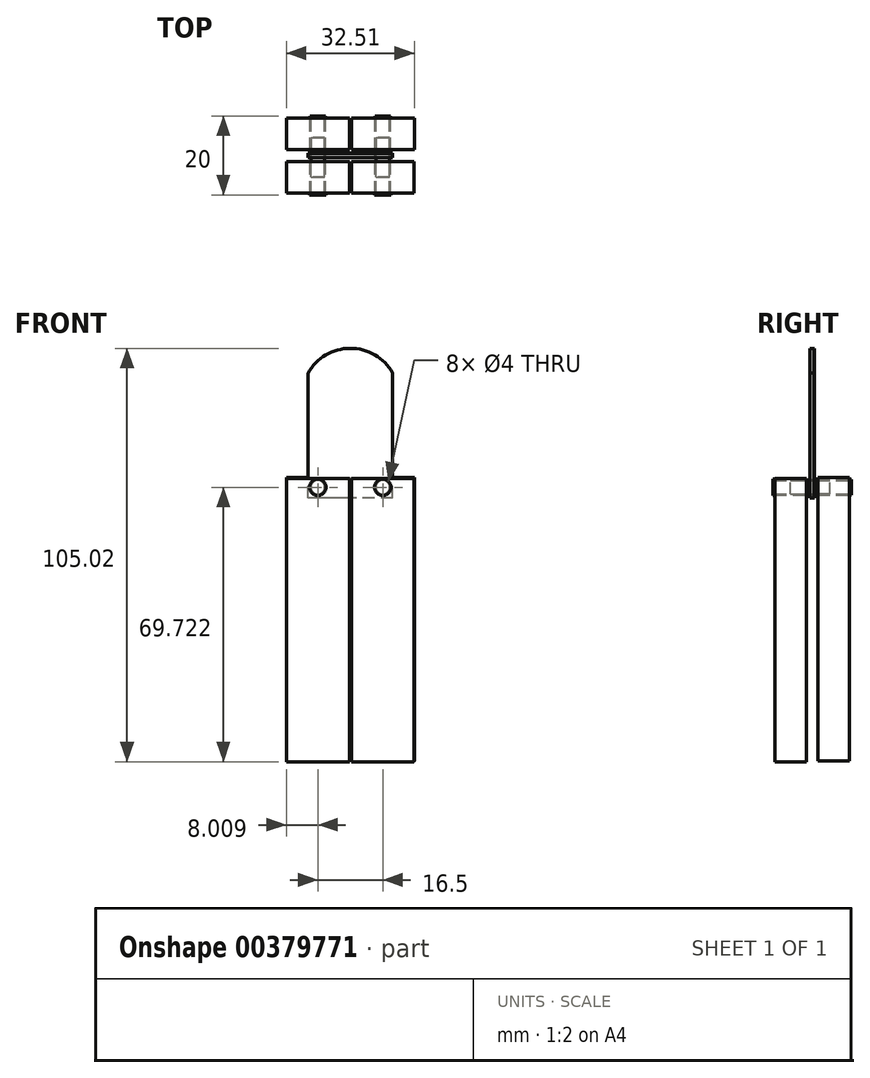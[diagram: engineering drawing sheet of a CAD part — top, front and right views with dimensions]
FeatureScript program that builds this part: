
annotation { "Feature Type Name" : "Feature", "Feature Type Description" : "" }
export const myFeature = defineFeature(function(context is Context, id is Id, definition is map)
    precondition{}
    {
        {
            var Q0;
            Q0=qCreatedBy(makeId("Front.planeOp"),FACE);
            var sketch = newSketch(context, id + "F0", { "sketchPlane" : qUnion([Q0])});
            skLineSegment(sketch, "E0.bottom", {"start": v(-36.14, 39.08) * mm, "end": v(-20.14, 39.08) * mm});
            skLineSegment(sketch, "E0.top", {"start": v(-36.14, -32.92) * mm, "end": v(-20.14, -32.92) * mm});
            skLineSegment(sketch, "E0.left", {"start": v(-36.14, 39.08) * mm, "end": v(-36.14, -32.92) * mm});
            skLineSegment(sketch, "E0.right", {"start": v(-20.14, 39.08) * mm, "end": v(-20.14, -32.92) * mm});
            skLineSegment(sketch, "E1.bottom", {"start": v(-19.64, 39.08) * mm, "end": v(-3.64, 39.08) * mm});
            skLineSegment(sketch, "E1.top", {"start": v(-19.64, -32.92) * mm, "end": v(-3.64, -32.92) * mm});
            skLineSegment(sketch, "E1.left", {"start": v(-19.64, 39.08) * mm, "end": v(-19.64, -32.92) * mm});
            skLineSegment(sketch, "E1.right", {"start": v(-3.64, 39.08) * mm, "end": v(-3.64, -32.92) * mm});
            skSolve(sketch);
        }
        {
            var Q0;
            Q0=makeQuery(id+"F0.imprint","IMPRINT",FACE,{"disambiguationData":[TD([[makeQuery(id+"F0.imprint","IMPRINT",EDGE,{"derivedFrom":sQuery(id+"F0.wireOp",EDGE,"E0.bottom")}),-1.0]])]});
            var Q1;
            Q1=makeQuery(id+"F0.imprint","IMPRINT",FACE,{"disambiguationData":[TD([[makeQuery(id+"F0.imprint","IMPRINT",EDGE,{"derivedFrom":sQuery(id+"F0.wireOp",EDGE,"E1.bottom")}),-1.0]])]});
            extrude(context, id + "F1", {"entities" : qUnion([Q0, Q1]), "depth" : 8 * mm});
        }
        {
            var Q0;
            Q0=makeQuery(id+"F1.opExtrude","CAP_FACE",FACE,{"disambiguationData":[OSD([sQuery(id+"F0.wireOp",EDGE,"E1.bottom"),sQuery(id+"F0.wireOp",EDGE,"E1.top"),sQuery(id+"F0.wireOp",EDGE,"E1.left"),sQuery(id+"F0.wireOp",EDGE,"E1.right")])],"isStart":true});
            var sketch = newSketch(context, id + "F2", { "sketchPlane" : qUnion([Q0])});
            skCircle(sketch, "E2", {"center": v(11.64, 36.58) * mm, "radius": 1.5 * mm});
            skCircle(sketch, "E3", {"center": v(28.14, 36.58) * mm, "radius": 1.5 * mm});
            skCircle(sketch, "E4", {"center": v(28.14, 36.58) * mm, "radius": 1.75 * mm});
            skCircle(sketch, "E5", {"center": v(11.64, 36.58) * mm, "radius": 1.75 * mm});
            skCircle(sketch, "E6", {"center": v(11.64, 36.58) * mm, "radius": 2 * mm});
            skCircle(sketch, "E7", {"center": v(28.14, 36.58) * mm, "radius": 2 * mm});
            skSolve(sketch);
        }
        {
            var Q0;
            Q0 = qSketchRegion(id + "F2", true);
            extrude(context, id + "F3", {"entities" : qUnion([Q0]), "oppositeDirection" : true, "depth" : 11 * mm});
        }
        {
            var Q0;
            Q0=qCreatedBy(makeId("Front.planeOp"),FACE);
            cPlane(context, id + "F4", {"entities" : qUnion([Q0]), "cplaneType" : CPlaneType.OFFSET, "offset" : 9 * mm, "width" : 150 * mm, "height" : 150 * mm});
        }
        {
            var Q0;
            Q0=qCreatedBy(id+"F4.planeOp",FACE);
            var sketch = newSketch(context, id + "F5", { "sketchPlane" : qUnion([Q0])});
            skLineSegment(sketch, "E8", {"start": v(-30.64, 33.85) * mm, "end": v(-30.64, 65.54) * mm});
            skLineSegment(sketch, "E9", {"start": v(-9.14, 33.88) * mm, "end": v(-9.14, 65.6) * mm});
            skArc(sketch, "E10", {"start": v(-9.14, 65.6) * mm, "mid": v(-19.9, 71.88) * mm, "end": v(-30.64, 65.54) * mm});
            skLineSegment(sketch, "E11", {"start": v(-9.14, 33.88) * mm, "end": v(-30.64, 33.88) * mm});
            skLineSegment(sketch, "E12", {"start": v(-30.64, 33.85) * mm, "end": v(-30.64, 33.88) * mm});
            skSolve(sketch);
        }
        {
            var Q0;
            Q0=makeQuery(id+"F5.imprint","IMPRINT",FACE,{"disambiguationData":[TD([[makeQuery(id+"F5.imprint","IMPRINT",EDGE,{"derivedFrom":sQuery(id+"F5.wireOp",EDGE,"E8")}),-1.0]])]});
            extrude(context, id + "F6", {"entities" : qUnion([Q0]), "operationType" : NewBodyOperationType.ADD, "depth" : 1 * mm});
        }
        {
            var Q0;
            Q0=qCreatedBy(id+"F4.planeOp",FACE);
            cPlane(context, id + "F7", {"entities" : qUnion([Q0]), "cplaneType" : CPlaneType.OFFSET, "offset" : 2 * mm, "width" : 150 * mm, "height" : 150 * mm});
        }
        {
            var Q0;
            Q0=qCreatedBy(id+"F7.planeOp",FACE);
            cPlane(context, id + "F8", {"entities" : qUnion([Q0]), "cplaneType" : CPlaneType.OFFSET, "offset" : 10 * mm, "width" : 150 * mm, "height" : 150 * mm});
        }
        {
            var Q0;
            Q0=qCreatedBy(id+"F8.planeOp",FACE);
            var sketch = newSketch(context, id + "F9", { "sketchPlane" : qUnion([Q0])});
            skLineSegment(sketch, "E13.bottom", {"start": v(-36.15, 38.86) * mm, "end": v(-20.15, 38.86) * mm});
            skLineSegment(sketch, "E13.top", {"start": v(-36.15, -33.14) * mm, "end": v(-20.15, -33.14) * mm});
            skLineSegment(sketch, "E13.left", {"start": v(-36.15, 38.86) * mm, "end": v(-36.15, -33.14) * mm});
            skLineSegment(sketch, "E13.right", {"start": v(-20.15, 38.86) * mm, "end": v(-20.15, -33.14) * mm});
            skLineSegment(sketch, "E14.bottom", {"start": v(-3.65, 38.86) * mm, "end": v(-19.65, 38.86) * mm});
            skLineSegment(sketch, "E14.top", {"start": v(-3.65, -33.14) * mm, "end": v(-19.65, -33.14) * mm});
            skLineSegment(sketch, "E14.left", {"start": v(-3.65, 38.86) * mm, "end": v(-3.65, -33.14) * mm});
            skLineSegment(sketch, "E14.right", {"start": v(-19.65, 38.86) * mm, "end": v(-19.65, -33.14) * mm});
            skSolve(sketch);
        }
        {
            var Q0;
            Q0=makeQuery(id+"F9.imprint","IMPRINT",FACE,{"disambiguationData":[TD([[makeQuery(id+"F9.imprint","IMPRINT",EDGE,{"derivedFrom":sQuery(id+"F9.wireOp",EDGE,"E13.bottom")}),-1.0]])]});
            var Q1;
            Q1=makeQuery(id+"F9.imprint","IMPRINT",FACE,{"disambiguationData":[TD([[makeQuery(id+"F9.imprint","IMPRINT",EDGE,{"derivedFrom":sQuery(id+"F9.wireOp",EDGE,"E14.bottom")}),1.0]])]});
            extrude(context, id + "F10", {"entities" : qUnion([Q0, Q1]), "oppositeDirection" : true, "depth" : 10 * mm});
        }
        {
            var Q0;
            Q0=makeQuery(id+"F10.opExtrude","CAP_FACE",FACE,{"disambiguationData":[OSD([sQuery(id+"F9.wireOp",EDGE,"E13.bottom"),sQuery(id+"F9.wireOp",EDGE,"E13.top"),sQuery(id+"F9.wireOp",EDGE,"E13.left"),sQuery(id+"F9.wireOp",EDGE,"E13.right")])],"isStart":true});
            var Q1;
            Q1=makeQuery(id+"F10.opExtrude","CAP_FACE",FACE,{"disambiguationData":[OSD([sQuery(id+"F9.wireOp",EDGE,"E14.bottom"),sQuery(id+"F9.wireOp",EDGE,"E14.top"),sQuery(id+"F9.wireOp",EDGE,"E14.left"),sQuery(id+"F9.wireOp",EDGE,"E14.right")])],"isStart":true});
            extrude(context, id + "F11", {"entities" : qUnion([Q0, Q1]), "operationType" : NewBodyOperationType.REMOVE, "oppositeDirection" : true, "depth" : 2 * mm});
        }
        {
            var Q0;
            Q0=makeQuery(id+"F3.opExtrude","CAP_FACE",FACE,{"disambiguationData":[OSD([sQuery(id+"F2.wireOp",EDGE,"E3"),sQuery(id+"F2.wireOp",EDGE,"E4")])],"isStart":true});
            var Q1;
            Q1=makeQuery(id+"F3.opExtrude","CAP_FACE",FACE,{"disambiguationData":[OSD([sQuery(id+"F2.wireOp",EDGE,"E2"),sQuery(id+"F2.wireOp",EDGE,"E5")])],"isStart":true});
            extrude(context, id + "F12", {"entities" : qUnion([Q0, Q1]), "operationType" : NewBodyOperationType.REMOVE, "oppositeDirection" : true, "depth" : 8.5 * mm});
        }
        {
            var Q0;
            {var subQ0=sQuery(id+"F5.wireOp",EDGE,"E8");var subQ1=sQuery(id+"F5.wireOp",EDGE,"E9");var subQ2=sQuery(id+"F5.wireOp",EDGE,"E10");var subQ3=sQuery(id+"F5.wireOp",EDGE,"E11");Q0=makeQuery(id+"F6.boolean.opBoolean","SPLIT",FACE,{"disambiguationData":[TD([makeQuery(id+"F3.opExtrude","SWEPT_FACE",FACE,{"disambiguationData":[OSD([sQuery(id+"F2.wireOp",EDGE,"E6")])]})])],"derivedFrom":makeQuery(id+"F6.opExtrude","CAP_FACE",FACE,{"disambiguationData":[OSD([subQ0,subQ1,subQ2,subQ3])],"isStart":true})});}
            extrude(context, id + "F13", {"entities" : qUnion([Q0]), "depth" : .1 * mm});
        }
        {
            var Q0;
            Q0=makeQuery(id+"F6.boolean.opBoolean","SPLIT",FACE,{"disambiguationData":[TD([makeQuery(id+"F3.opExtrude","SWEPT_FACE",FACE,{"disambiguationData":[OSD([sQuery(id+"F2.wireOp",EDGE,"E5")])]})])],"derivedFrom":makeQuery(id+"F6.opExtrude","CAP_FACE",FACE,{"disambiguationData":[OSD([sQuery(id+"F5.wireOp",EDGE,"E8"),sQuery(id+"F5.wireOp",EDGE,"E9"),sQuery(id+"F5.wireOp",EDGE,"E10"),sQuery(id+"F5.wireOp",EDGE,"E11")])],"isStart":true})});
            var Q1;
            Q1=makeQuery(id+"F6.boolean.opBoolean","SPLIT",FACE,{"disambiguationData":[TD([makeQuery(id+"F3.opExtrude","SWEPT_FACE",FACE,{"disambiguationData":[OSD([sQuery(id+"F2.wireOp",EDGE,"E4")])]})])],"derivedFrom":makeQuery(id+"F6.opExtrude","CAP_FACE",FACE,{"disambiguationData":[OSD([sQuery(id+"F5.wireOp",EDGE,"E8"),sQuery(id+"F5.wireOp",EDGE,"E9"),sQuery(id+"F5.wireOp",EDGE,"E10"),sQuery(id+"F5.wireOp",EDGE,"E11")])],"isStart":true})});
            extrude(context, id + "F14", {"entities" : qUnion([Q0, Q1]), "depth" : 4 * mm});
        }
        {
            var Q0;
            Q0=makeQuery(id+"F12.boolean.opBoolean","COPY",FACE,{"derivedFrom":makeQuery(id+"F12.opExtrude","CAP_FACE",FACE,{"disambiguationData":[OSD([sQuery(id+"F2.wireOp",EDGE,"E3"),sQuery(id+"F2.wireOp",EDGE,"E4")])],"isStart":false})});
            var Q1;
            Q1=makeQuery(id+"F12.boolean.opBoolean","COPY",FACE,{"derivedFrom":makeQuery(id+"F12.opExtrude","CAP_FACE",FACE,{"disambiguationData":[OSD([sQuery(id+"F2.wireOp",EDGE,"E2"),sQuery(id+"F2.wireOp",EDGE,"E5")])],"isStart":false})});
            extrude(context, id + "F15", {"entities" : qUnion([Q0, Q1]), "operationType" : NewBodyOperationType.REMOVE, "oppositeDirection" : true, "depth" : 25 * mm});
        }
        {
            var Q0;
            Q0=makeQuery(id+"F6.boolean.opBoolean","SPLIT",FACE,{"disambiguationData":[TD([makeQuery(id+"F3.opExtrude","SWEPT_FACE",FACE,{"disambiguationData":[OSD([sQuery(id+"F2.wireOp",EDGE,"E4")])]})])],"derivedFrom":makeQuery(id+"F6.opExtrude","CAP_FACE",FACE,{"disambiguationData":[OSD([sQuery(id+"F5.wireOp",EDGE,"E8"),sQuery(id+"F5.wireOp",EDGE,"E9"),sQuery(id+"F5.wireOp",EDGE,"E10"),sQuery(id+"F5.wireOp",EDGE,"E11")])],"isStart":false})});
            var Q1;
            Q1=makeQuery(id+"F6.boolean.opBoolean","SPLIT",FACE,{"disambiguationData":[TD([makeQuery(id+"F3.opExtrude","SWEPT_FACE",FACE,{"disambiguationData":[OSD([sQuery(id+"F2.wireOp",EDGE,"E5")])]})])],"derivedFrom":makeQuery(id+"F6.opExtrude","CAP_FACE",FACE,{"disambiguationData":[OSD([sQuery(id+"F5.wireOp",EDGE,"E8"),sQuery(id+"F5.wireOp",EDGE,"E9"),sQuery(id+"F5.wireOp",EDGE,"E10"),sQuery(id+"F5.wireOp",EDGE,"E11")])],"isStart":false})});
            extrude(context, id + "F16", {"entities" : qUnion([Q0, Q1]), "depth" : 5 * mm});
        }
        {
            var Q0;
            Q0=makeQuery(id+"F2.imprint","IMPRINT",FACE,{"disambiguationData":[TD([[makeQuery(id+"F2.imprint","IMPRINT",EDGE,{"derivedFrom":sQuery(id+"F2.wireOp",EDGE,"E4")}),-1.0]])]});
            var Q1;
            Q1=makeQuery(id+"F2.imprint","IMPRINT",FACE,{"disambiguationData":[TD([[makeQuery(id+"F2.imprint","IMPRINT",EDGE,{"derivedFrom":sQuery(id+"F2.wireOp",EDGE,"E5")}),-1.0]])]});
            var Q2;
            Q2=makeQuery(id+"F12.boolean.opBoolean","SPLIT",FACE,{"disambiguationData":[TD([makeQuery(id+"F12.opExtrude","SWEPT_FACE",FACE,{"disambiguationData":[OSD([sQuery(id+"F2.wireOp",EDGE,"E5")])]})])],"derivedFrom":makeQuery(id+"F1.opExtrude","CAP_FACE",FACE,{"disambiguationData":[OSD([sQuery(id+"F0.wireOp",EDGE,"E1.bottom"),sQuery(id+"F0.wireOp",EDGE,"E1.top"),sQuery(id+"F0.wireOp",EDGE,"E1.left"),sQuery(id+"F0.wireOp",EDGE,"E1.right")])],"isStart":true})});
            var Q3;
            Q3=makeQuery(id+"F2.imprint","IMPRINT",FACE,{"disambiguationData":[TD([[makeQuery(id+"F2.imprint","IMPRINT",EDGE,{"derivedFrom":sQuery(id+"F2.wireOp",EDGE,"E3")}),1.0]])]});
            var Q4;
            Q4=makeQuery(id+"F2.imprint","IMPRINT",FACE,{"disambiguationData":[TD([[makeQuery(id+"F2.imprint","IMPRINT",EDGE,{"derivedFrom":sQuery(id+"F2.wireOp",EDGE,"E3")}),-1.0]])]});
            extrude(context, id + "F17", {"entities" : qUnion([Q0, Q1, Q2, Q3, Q4]), "operationType" : NewBodyOperationType.ADD, "depth" : .5 * mm});
        }
        {
            var Q0;
            {var subQ0=sQuery(id+"F9.wireOp",EDGE,"E13.left");var subQ1=sQuery(id+"F9.wireOp",EDGE,"E13.top");var subQ2=sQuery(id+"F9.wireOp",EDGE,"E13.right");var subQ3=sQuery(id+"F9.wireOp",EDGE,"E13.bottom");Q0=makeQuery(id+"F15.boolean.opBoolean","SPLIT",FACE,{"disambiguationData":[TD([makeQuery(id+"F10.opExtrude","SWEPT_FACE",FACE,{"disambiguationData":[OSD([subQ3])]})])],"derivedFrom":makeQuery(id+"F11.boolean.opBoolean","COPY",FACE,{"derivedFrom":makeQuery(id+"F11.opExtrude","CAP_FACE",FACE,{"disambiguationData":[OSD([subQ3,subQ1,subQ0,subQ2])],"isStart":false})})});}
            var sketch = newSketch(context, id + "F18", { "sketchPlane" : qUnion([Q0])});
            skCircle(sketch, "E15", {"center": v(-28.14, 36.58) * mm, "radius": 2.1 * mm});
            skCircle(sketch, "E16", {"center": v(-11.65, 36.58) * mm, "radius": 2.1 * mm});
            skSolve(sketch);
        }
        {
            var Q0;
            Q0=makeQuery(id+"F18.imprint","IMPRINT",FACE,{"disambiguationData":[TD([[makeQuery(id+"F18.imprint","IMPRINT",EDGE,{"derivedFrom":sQuery(id+"F18.wireOp",EDGE,"E15")}),1.0]])]});
            var Q1;
            Q1=makeQuery(id+"F18.imprint","IMPRINT",FACE,{"disambiguationData":[TD([[makeQuery(id+"F18.imprint","IMPRINT",EDGE,{"derivedFrom":makeQuery(id+"F15.boolean.opBoolean","INTERSECT",EDGE,{"derivedFrom":[makeQuery(id+"F11.boolean.opBoolean","COPY",FACE,{"derivedFrom":makeQuery(id+"F11.opExtrude","CAP_FACE",FACE,{"disambiguationData":[OSD([sQuery(id+"F9.wireOp",EDGE,"E13.bottom"),sQuery(id+"F9.wireOp",EDGE,"E13.top"),sQuery(id+"F9.wireOp",EDGE,"E13.left"),sQuery(id+"F9.wireOp",EDGE,"E13.right")])],"isStart":false})}),makeQuery(id+"F15.opExtrude","SWEPT_FACE",FACE,{"disambiguationData":[OSD([sQuery(id+"F2.wireOp",EDGE,"E7")])]})]})}),1.0]])]});
            var Q2;
            Q2=makeQuery(id+"F18.imprint","IMPRINT",FACE,{"disambiguationData":[TD([[makeQuery(id+"F18.imprint","IMPRINT",EDGE,{"derivedFrom":sQuery(id+"F18.wireOp",EDGE,"E16")}),1.0]])]});
            extrude(context, id + "F19", {"entities" : qUnion([Q0, Q1, Q2]), "depth" : .5 * mm});
        }
    });
